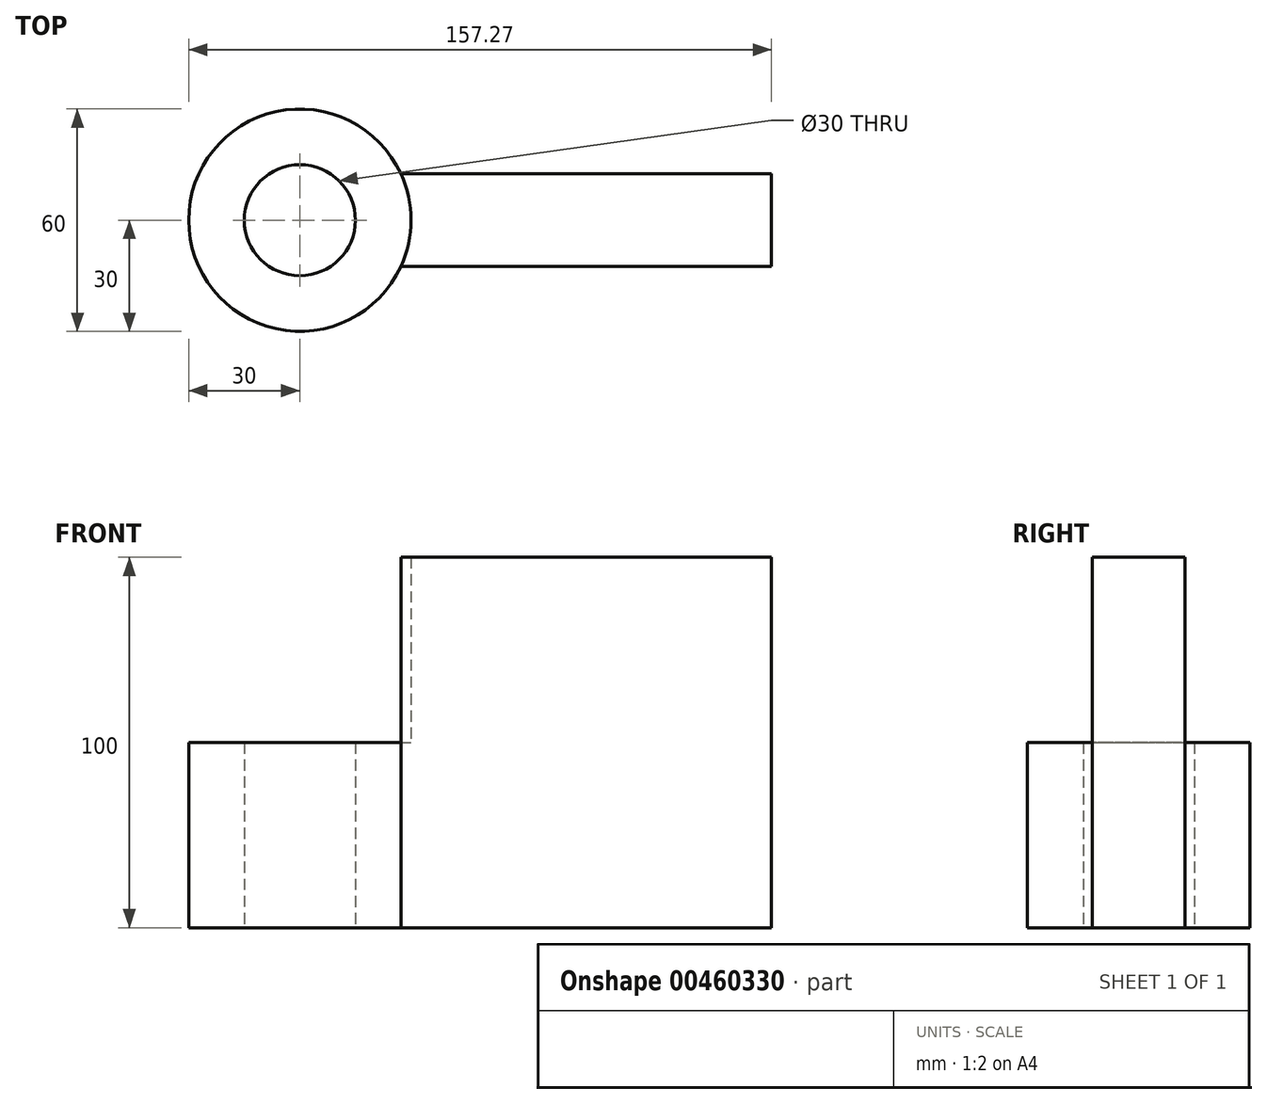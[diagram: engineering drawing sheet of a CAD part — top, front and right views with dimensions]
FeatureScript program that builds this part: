
annotation { "Feature Type Name" : "Feature", "Feature Type Description" : "" }
export const myFeature = defineFeature(function(context is Context, id is Id, definition is map)
    precondition{}
    {
        {
            var Q0;
            Q0=qCreatedBy(makeId("Top.planeOp"),FACE);
            var sketch = newSketch(context, id + "F0", { "sketchPlane" : qUnion([Q0])});
            skCircle(sketch, "E0", {"center": v(0, 0) * mm, "radius": 30 * mm});
            skCircle(sketch, "E1", {"center": v(0, 0) * mm, "radius": 15 * mm});
            skLineSegment(sketch, "E2", {"start": v(27.27, 12.5) * mm, "end": v(127.27, 12.5) * mm});
            skLineSegment(sketch, "E3", {"start": v(27.27, 12.5) * mm, "end": v(27.27, -12.5) * mm, "construction": true});
            skLineSegment(sketch, "E4", {"start": v(27.27, -12.5) * mm, "end": v(127.27, -12.5) * mm});
            skLineSegment(sketch, "E5", {"start": v(127.27, -12.5) * mm, "end": v(127.27, 12.5) * mm});
            skSolve(sketch);
        }
        {
            var Q0;
            Q0=makeQuery(id+"F0.imprint","IMPRINT",FACE,{"disambiguationData":[TD([[makeQuery(id+"F0.imprint","IMPRINT",EDGE,{"derivedFrom":sQuery(id+"F0.wireOp",EDGE,"E1")}),-1.0]])]});
            extrude(context, id + "F1", {"entities" : qUnion([Q0]), "depth" : 50 * mm});
        }
        {
            var Q0;
            {var subQ0=sQuery(id+"F0.wireOp",EDGE,"E2");Q0=makeQuery(id+"F0.imprint","IMPRINT",FACE,{"disambiguationData":[TD([[makeQuery(id+"F0.imprint","IMPRINT",EDGE,{"derivedFrom":subQ0}),-1.0]])]});}
            extrude(context, id + "F2", {"entities" : qUnion([Q0]), "operationType" : NewBodyOperationType.ADD, "depth" : 100 * mm});
        }
    });
